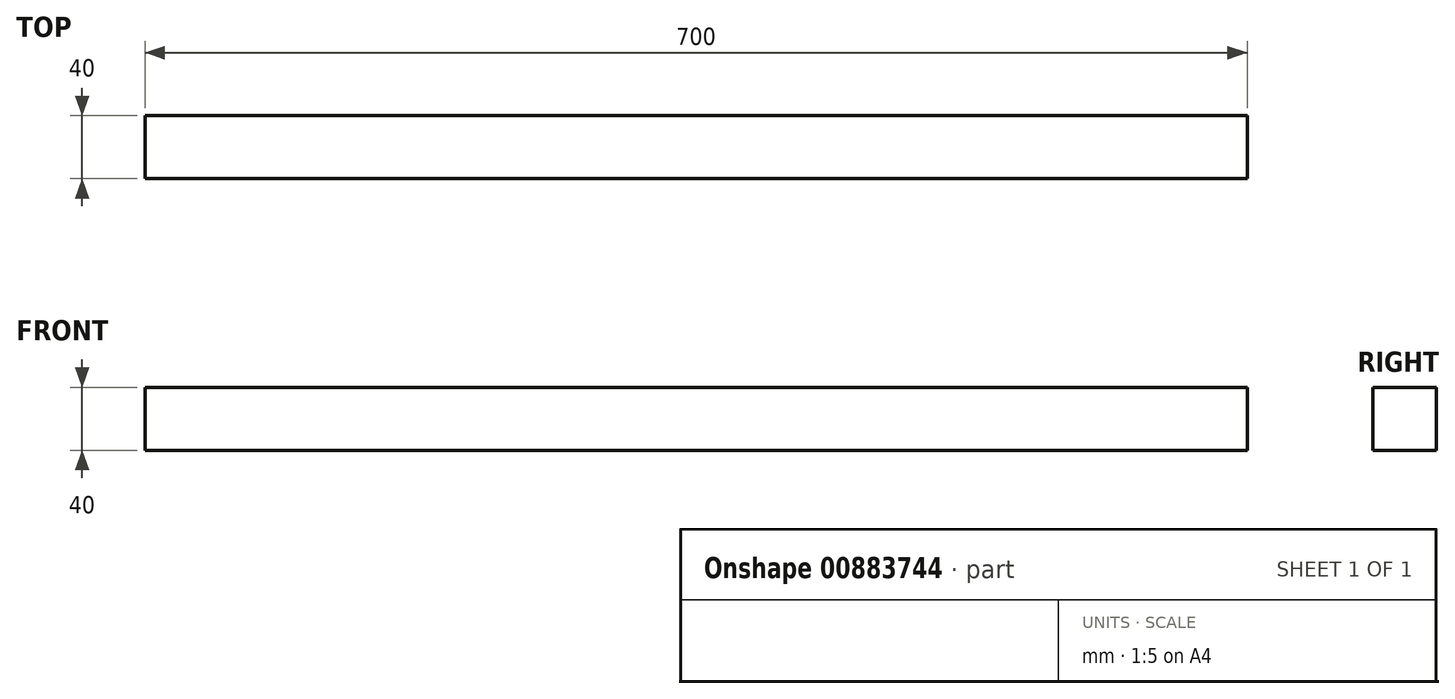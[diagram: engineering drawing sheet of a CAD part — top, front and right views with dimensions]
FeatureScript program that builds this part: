
annotation { "Feature Type Name" : "Feature", "Feature Type Description" : "" }
export const myFeature = defineFeature(function(context is Context, id is Id, definition is map)
    precondition{}
    {
        {
            var Q0;
            Q0=qCreatedBy(makeId("Right.planeOp"),FACE);
            var sketch = newSketch(context, id + "F0", { "sketchPlane" : qUnion([Q0])});
            skLineSegment(sketch, "E0.bottom", {"start": v(109.65, 4.94) * mm, "end": v(149.65, 4.94) * mm});
            skLineSegment(sketch, "E0.top", {"start": v(109.65, 44.94) * mm, "end": v(149.65, 44.94) * mm});
            skLineSegment(sketch, "E0.left", {"start": v(109.65, 4.94) * mm, "end": v(109.65, 44.94) * mm});
            skLineSegment(sketch, "E0.right", {"start": v(149.65, 4.94) * mm, "end": v(149.65, 44.94) * mm});
            skPoint(sketch, "E0.middle", {"position": v(129.65, 24.94) * mm});
            skSolve(sketch);
        }
        {
            var Q0;
            Q0 = qSketchRegion(id + "F0", true);
            extrude(context, id + "F1", {"entities" : qUnion([Q0]), "depth" : 700 * mm, "offsetDistance" : 25 * mm});
        }
    });
